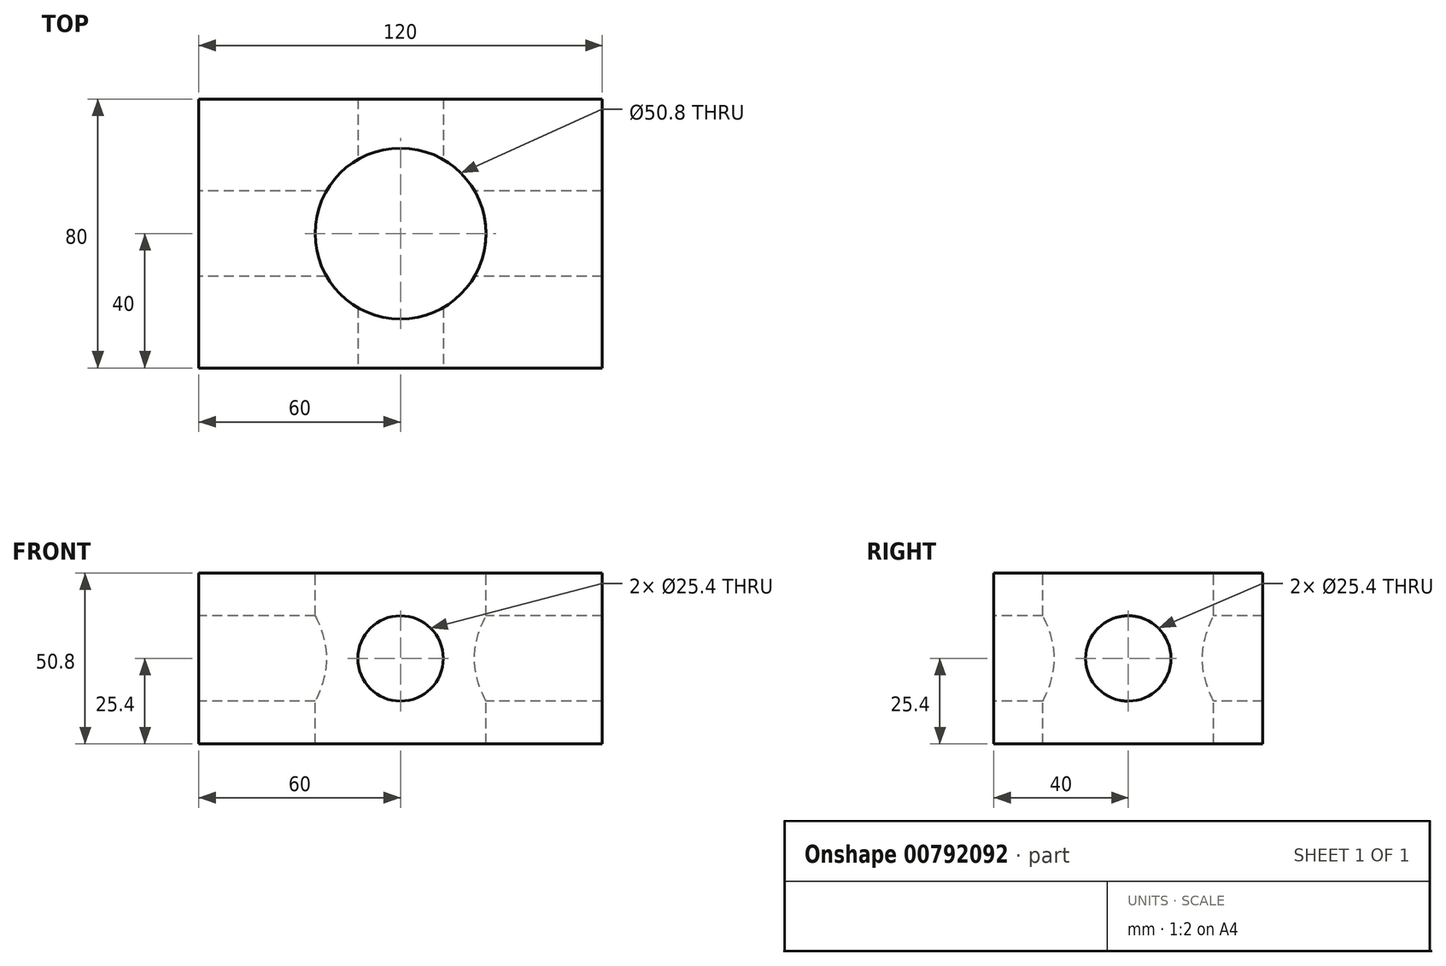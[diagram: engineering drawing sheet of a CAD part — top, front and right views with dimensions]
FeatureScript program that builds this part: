
annotation { "Feature Type Name" : "Feature", "Feature Type Description" : "" }
export const myFeature = defineFeature(function(context is Context, id is Id, definition is map)
    precondition{}
    {
        {
            var Q0;
            Q0=qCreatedBy(makeId("Top.planeOp"),FACE);
            var sketch = newSketch(context, id + "F0", { "sketchPlane" : qUnion([Q0])});
            skLineSegment(sketch, "E0.bottom", {"start": v(60, -40) * mm, "end": v(-60, -40) * mm});
            skLineSegment(sketch, "E0.top", {"start": v(60, 40) * mm, "end": v(-60, 40) * mm});
            skLineSegment(sketch, "E0.left", {"start": v(60, -40) * mm, "end": v(60, 40) * mm});
            skLineSegment(sketch, "E0.right", {"start": v(-60, -40) * mm, "end": v(-60, 40) * mm});
            skPoint(sketch, "E0.middle", {"position": v(0, 0) * mm});
            skSolve(sketch);
        }
        {
            var Q0;
            Q0=makeQuery(id+"F0.imprint","IMPRINT",FACE,{"disambiguationData":[TD([[makeQuery(id+"F0.imprint","IMPRINT",EDGE,{"derivedFrom":sQuery(id+"F0.wireOp",EDGE,"E0.bottom")}),-1.0]])]});
            extrude(context, id + "F1", {"entities" : qUnion([Q0]), "depth" : 25.4 * mm, "offsetDistance" : 25.4 * mm, "hasSecondDirection" : true, "secondDirectionOppositeDirection" : true, "secondDirectionDepth" : 25.4 * mm});
        }
        {
            var Q0;
            Q0=makeQuery(id+"F1.opExtrude","CAP_FACE",FACE,{"disambiguationData":[OSD([sQuery(id+"F0.wireOp",EDGE,"E0.bottom"),sQuery(id+"F0.wireOp",EDGE,"E0.top"),sQuery(id+"F0.wireOp",EDGE,"E0.left"),sQuery(id+"F0.wireOp",EDGE,"E0.right")])],"isStart":false});
            var sketch = newSketch(context, id + "F2", { "sketchPlane" : qUnion([Q0])});
            skCircle(sketch, "E1", {"center": v(0, 0) * mm, "radius": 25.4 * mm});
            skSolve(sketch);
        }
        {
            var Q0;
            Q0=sQuery(id+"F2.wireOp",VERTEX,"E1.center");
            var Q1;
            Q1=makeQuery(id+"F1.opExtrude","SWEPT_BODY",BODY,{"disambiguationData":[OSD([sQuery(id+"F0.wireOp",EDGE,"E0.bottom"),sQuery(id+"F0.wireOp",EDGE,"E0.top"),sQuery(id+"F0.wireOp",EDGE,"E0.left"),sQuery(id+"F0.wireOp",EDGE,"E0.right")])]});
            hole(context, id + "F3", {"style" : HoleStyle.SIMPLE, "endStyle" : HoleEndStyle.THROUGH, "holeDiameter" : 50.8 * mm, "majorDiameter" : 6.35 * mm, "isTappedThrough" : true, "tappedDepth" : 12.7 * mm, "tapClearance" : 3, "locations" : qUnion([Q0]), "scope" : qUnion([Q1])});
        }
        {
            var Q0;
            Q0=makeQuery(id+"F1.opExtrude","SWEPT_FACE",FACE,{"disambiguationData":[OSD([sQuery(id+"F0.wireOp",EDGE,"E0.bottom")])]});
            var sketch = newSketch(context, id + "F4", { "sketchPlane" : qUnion([Q0])});
            skCircle(sketch, "E2", {"center": v(0, 0) * mm, "radius": 12.7 * mm});
            skSolve(sketch);
        }
        {
            var Q0;
            Q0=sQuery(id+"F4.wireOp",VERTEX,"E2.center");
            var Q1;
            Q1=makeQuery(id+"F1.opExtrude","SWEPT_BODY",BODY,{"disambiguationData":[OSD([sQuery(id+"F0.wireOp",EDGE,"E0.bottom"),sQuery(id+"F0.wireOp",EDGE,"E0.top"),sQuery(id+"F0.wireOp",EDGE,"E0.left"),sQuery(id+"F0.wireOp",EDGE,"E0.right")])]});
            hole(context, id + "F5", {"style" : HoleStyle.SIMPLE, "endStyle" : HoleEndStyle.THROUGH, "holeDiameter" : 25.4 * mm, "majorDiameter" : 6.35 * mm, "isTappedThrough" : true, "tappedDepth" : 12.7 * mm, "tapClearance" : 3, "locations" : qUnion([Q0]), "scope" : qUnion([Q1])});
        }
        {
            var Q0;
            Q0=makeQuery(id+"F1.opExtrude","SWEPT_FACE",FACE,{"disambiguationData":[OSD([sQuery(id+"F0.wireOp",EDGE,"E0.right")])]});
            var sketch = newSketch(context, id + "F6", { "sketchPlane" : qUnion([Q0])});
            skCircle(sketch, "E3", {"center": v(0, 0) * mm, "radius": 12.7 * mm});
            skSolve(sketch);
        }
        {
            var Q0;
            Q0=sQuery(id+"F6.wireOp",VERTEX,"E3.center");
            var Q1;
            Q1=makeQuery(id+"F1.opExtrude","SWEPT_BODY",BODY,{"disambiguationData":[OSD([sQuery(id+"F0.wireOp",EDGE,"E0.bottom"),sQuery(id+"F0.wireOp",EDGE,"E0.top"),sQuery(id+"F0.wireOp",EDGE,"E0.left"),sQuery(id+"F0.wireOp",EDGE,"E0.right")])]});
            hole(context, id + "F7", {"style" : HoleStyle.SIMPLE, "endStyle" : HoleEndStyle.THROUGH, "holeDiameter" : 25.4 * mm, "majorDiameter" : 6.35 * mm, "isTappedThrough" : true, "tappedDepth" : 12.7 * mm, "tapClearance" : 3, "locations" : qUnion([Q0]), "scope" : qUnion([Q1])});
        }
    });
